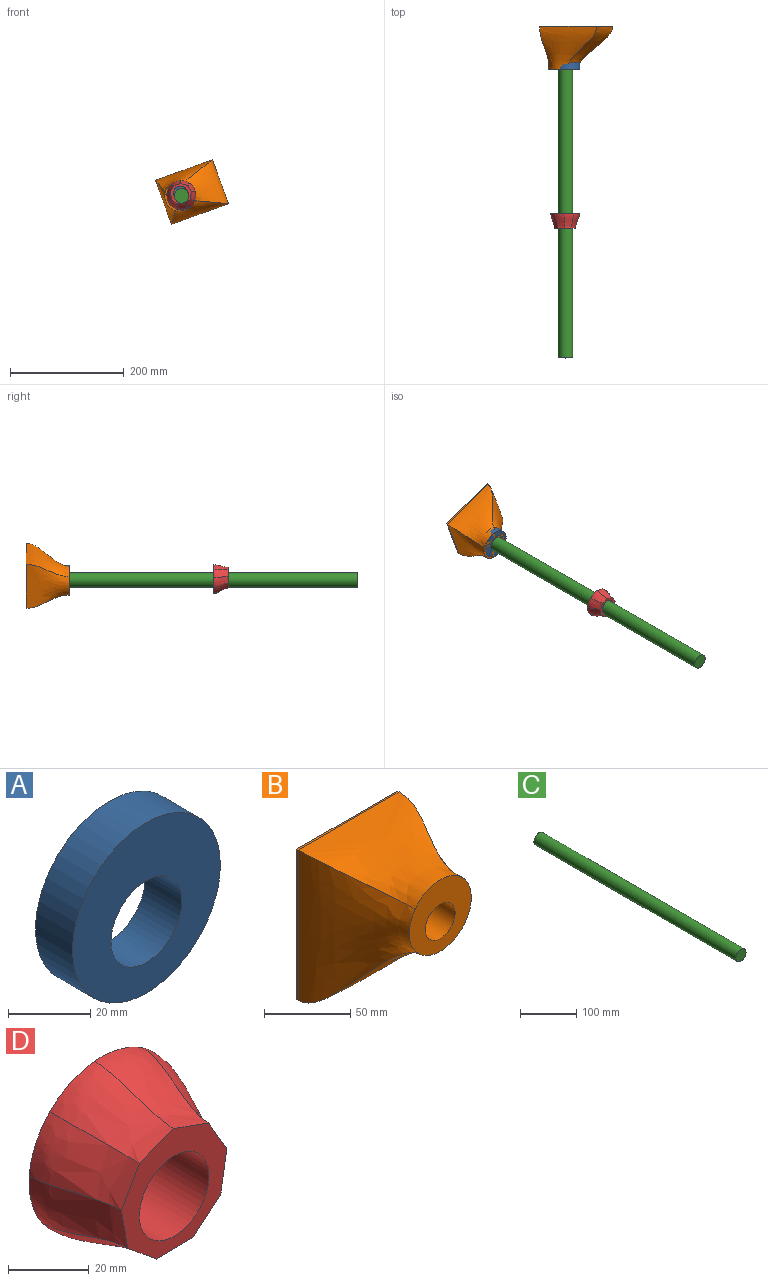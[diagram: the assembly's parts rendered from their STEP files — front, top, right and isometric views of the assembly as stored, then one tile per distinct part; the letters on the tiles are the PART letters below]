
ASSEMBLY  parts=4 mates=3
PART A: 4 faces, bbox 50.8x12.7x50.8 mm
  f0: cylinder r=25.38mm len=50.75mm, axis (0,1,0), area 2024.9mm2, adj f1,f2
  f1: plane 50.75x50.75mm, normal (0,-1,0), area 1557.6mm2, adj f0,f3
  f2: plane 50.75x50.75mm, normal (0,1,0), area 1557.6mm2, adj f0,f3
  f3: cylinder r=12.17mm len=24.34mm, axis (0,-1,0), area 971.2mm2, adj f1,f2
PART B: 11 faces, bbox 82.4x76.2x106.4 mm
  f0: plane 106.44x1.27mm, normal (-1,0,0), area 135.2mm2, adj f1,f3,f4,f6
  f1: plane 82.37x1.27mm, normal (0,0,-1), area 104.6mm2, adj f0,f2,f4,f7
  f2: plane 106.44x1.27mm, normal (1,0,0), area 135.2mm2, adj f1,f3,f4,f8
  f3: plane 82.37x1.27mm, normal (0,0,1), area 104.6mm2, adj f0,f2,f4,f9
  f4: plane 106.44x82.37mm, normal (0,1,0), area 8302.5mm2, adj f0,f1,f2,f3,f10
  f5: plane 50.77x50.77mm, normal (0,-1,0), area 1557.6mm2, adj f6,f7,f8,f9,f10
  f6: bspline ~106.44x74.93mm, area 5694.3mm2, adj f0,f5,f7,f9
  f7: bspline ~82.37x74.93mm, area 5749mm2, adj f1,f5,f6,f8
  f8: bspline ~106.44x74.93mm, area 5640.6mm2, adj f2,f5,f7,f9
  f9: bspline ~82.37x74.93mm, area 4560.7mm2, adj f3,f5,f6,f8
  f10: cylinder r=12.17mm len=76.2mm, axis (0,-1,0), area 5827.1mm2, adj f4,f5
PART C: 3 faces, bbox 25.5x508x25.5 mm
  f0: cylinder r=12.77mm len=508mm, axis (0,1,0), area 40746.1mm2, adj f1,f2
  f1: plane 25.53x25.53mm, normal (0,-1,0), area 512mm2, adj f0
  f2: plane 25.53x25.53mm, normal (0,1,0), area 512mm2, adj f0
PART D: 12 faces, bbox 51.1x25.4x51.1 mm
  f0: plane 50.83x50.83mm, normal (0,1,0), area 1557.5mm2, adj f2,f3,f4,f5,f6,f7,f8,f9
  f1: plane 36.96x36.43mm, normal (0,-1,0), area 553mm2, adj f2,f3,f4,f5,f6,f7,f8,f9
  f2: bspline ~25.4x17mm, area 411.2mm2, adj f0,f1,f3,f10
  f3: bspline ~25.4x16.73mm, area 403mm2, adj f0,f1,f2,f4
  f4: bspline ~25.4x14.34mm, area 397.4mm2, adj f0,f1,f3,f5
  f5: bspline ~25.4x17.28mm, area 395.7mm2, adj f0,f1,f4,f6
  f6: bspline ~25.4x16.57mm, area 398mm2, adj f0,f1,f5,f7
  f7: bspline ~25.4x18.44mm, area 404.3mm2, adj f0,f1,f6,f8
  f8: bspline ~25.4x19.92mm, area 412.5mm2, adj f0,f1,f7,f9
  f9: bspline ~25.4x16.81mm, area 418.1mm2, adj f0,f1,f8,f10
  f10: bspline ~25.4x17.99mm, area 417.6mm2, adj f0,f1,f2,f9
  f11: cylinder r=12.17mm len=25.4mm, axis (0,-1,0), area 1942.4mm2, adj f0,f1
PLACE A rot(axis=(0,-1,0),110deg) t=(-177.33,617.86,-72.79)mm
PLACE B rot(axis=(0,-1,0),110deg) t=(-181.19,605.16,-74.2)mm
PLACE C rot(axis=(-0.17,0,0.98),180deg) t=(-199.63,20.96,-80.91)mm
PLACE D rot(axis=(0,1,0),160deg) t=(-208.16,363.86,-57.46)mm
MATE fastened C.f0 <-> D.f0  axis (0,-1,0) through (-199.63,274.96,-80.91)mm
MATE fastened A.f0 <-> B.f10  axis (0,-1,0) through (-199.63,528.96,-80.91)mm
MATE slider B.f10 <-> C.f0  axis (0,1,0) through (-199.63,605.16,-80.91)mm
